# Revit family: DC_Holyoake_MEQ_LD-600_13
name_source: partatom
category: Air Terminals
revit_build: Autodesk Revit 2014 (Build: 20130308_1515(x64)
units: mm (PartAtom-declared; Revit-internal decimal feet)

## types (1)
- LD 600
    Default Elevation = 0 mm  [stored 0 ft]
    Description = Linear Bar Diffuser shall be Holyoake Model LD-600. Linear Bar Diffuser shall be 0 degrees deflection, of extruded aluminium construction to the sizes as documented and supplied. Diffusers shall be finished in powdercoat and fitted with accessories and dampers where indicated as manufactured by Holyoake.
    Holyoake Product Range = Holyoake Linear Bar Diffusers
    Manufacturer = Holyoake
    Material Body = Holyoake-Aluminium
    Material Face = Holyoake-Aluminium
    Max Flow = 1200 L/s
    Min Flow = 30 L/s
    Model = LD-600
    Noise Level NC Max = 44 NC
    Noise Level NC Min = < 10 NC
    Static Pressure Max = 69.00 Pa
    Static Pressure Min = 3.00 Pa
    Type Comments = Fineline Diffuser Series LD linear bar grilles
    URL = http://www.holyoake.com

note: [stored X ft] marks values corroborated as IEEE doubles in the binary element streams (Revit-internal decimal feet)

## geometry (parser evidence)
native form markers: Blend x6, Sweep x2
no freeform markers — native parametric forms only
